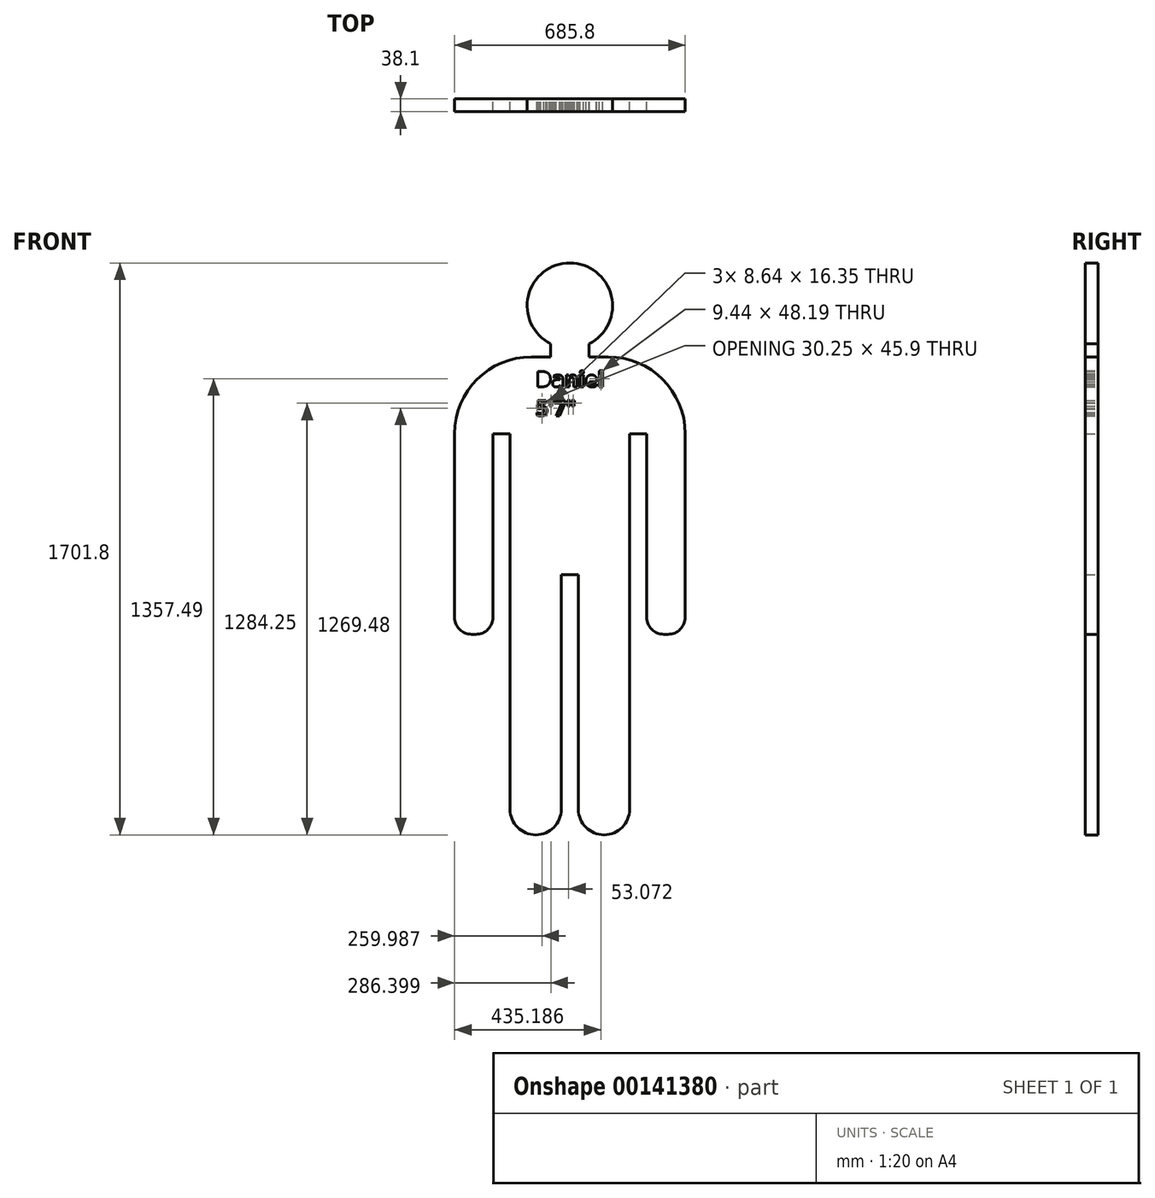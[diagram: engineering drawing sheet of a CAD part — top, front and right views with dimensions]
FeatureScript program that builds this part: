
annotation { "Feature Type Name" : "Feature", "Feature Type Description" : "" }
export const myFeature = defineFeature(function(context is Context, id is Id, definition is map)
    precondition{}
    {
        {
            var Q0;
            Q0=qCreatedBy(makeId("Front.planeOp"),FACE);
            var sketch = newSketch(context, id + "F0", { "sketchPlane" : qUnion([Q0])});
            skArc(sketch, "E0", {"start": v(48.02, 798.98) * mm, "mid": v(-9.13, 1039.4) * mm, "end": v(-66.28, 798.98) * mm});
            skLineSegment(sketch, "E1.bottom", {"start": v(-123.43, 760) * mm, "end": v(-66.28, 760) * mm});
            skLineSegment(sketch, "E1.top", {"start": v(-110.73, -662.4) * mm, "end": v(-110.73, -662.4) * mm});
            skLineSegment(sketch, "E1.left", {"start": v(-352.03, 531.4) * mm, "end": v(-352.03, -14.7) * mm});
            skLineSegment(sketch, "E1.right", {"start": v(333.77, 531.4) * mm, "end": v(333.77, -14.7) * mm});
            skPoint(sketch, "E2.visualSharp", {"position": v(-352.03, 760) * mm});
            skArc(sketch, "E2.filletArc", {"start": v(-345.68, 760) * mm, "mid": v(-350.17, 758.14) * mm, "end": v(-352.03, 753.65) * mm});
            skArc(sketch, "E3.filletArc", {"start": v(-123.43, 760) * mm, "mid": v(-285.08, 693.04) * mm, "end": v(-352.03, 531.4) * mm});
            skPoint(sketch, "E4.visualSharp", {"position": v(333.77, 760) * mm});
            skArc(sketch, "E4.filletArc", {"start": v(333.77, 531.4) * mm, "mid": v(266.81, 693.04) * mm, "end": v(105.17, 760) * mm});
            skLineSegment(sketch, "E5", {"start": v(-34.53, -586.2) * mm, "end": v(-34.53, 112.3) * mm});
            skLineSegment(sketch, "E6", {"start": v(16.27, 112.3) * mm, "end": v(16.27, -586.2) * mm});
            skLineSegment(sketch, "E7", {"start": v(-186.93, 531.4) * mm, "end": v(-186.93, -586.2) * mm});
            skLineSegment(sketch, "E8", {"start": v(168.67, 531.4) * mm, "end": v(168.67, -586.2) * mm});
            skLineSegment(sketch, "E9", {"start": v(-301.23, -65.5) * mm, "end": v(-288.53, -65.5) * mm});
            skLineSegment(sketch, "E10", {"start": v(-237.73, -14.7) * mm, "end": v(-237.73, 531.4) * mm});
            skLineSegment(sketch, "E11", {"start": v(-237.73, 531.4) * mm, "end": v(-186.93, 531.4) * mm});
            skLineSegment(sketch, "E12", {"start": v(168.67, 531.4) * mm, "end": v(219.47, 531.4) * mm});
            skLineSegment(sketch, "E13", {"start": v(219.47, 531.4) * mm, "end": v(219.47, -14.7) * mm});
            skLineSegment(sketch, "E14", {"start": v(270.27, -65.5) * mm, "end": v(282.97, -65.5) * mm});
            skPoint(sketch, "E15.orphan", {"position": v(-352.03, -662.4) * mm});
            skLineSegment(sketch, "E16.trimOffspring", {"start": v(92.47, -662.4) * mm, "end": v(92.47, -662.4) * mm});
            skPoint(sketch, "E17.orphan", {"position": v(333.77, -662.4) * mm});
            skLineSegment(sketch, "E18", {"start": v(16.27, 112.3) * mm, "end": v(-34.53, 112.3) * mm});
            skPoint(sketch, "E19.visualSharp", {"position": v(-352.03, -65.5) * mm});
            skArc(sketch, "E19.filletArc", {"start": v(-352.03, -14.7) * mm, "mid": v(-337.15, -50.62) * mm, "end": v(-301.23, -65.5) * mm});
            skPoint(sketch, "E20.visualSharp", {"position": v(-237.73, -65.5) * mm});
            skArc(sketch, "E20.filletArc", {"start": v(-288.53, -65.5) * mm, "mid": v(-252.6, -50.62) * mm, "end": v(-237.73, -14.7) * mm});
            skPoint(sketch, "E21.visualSharp", {"position": v(219.47, -65.5) * mm});
            skArc(sketch, "E21.filletArc", {"start": v(219.47, -14.7) * mm, "mid": v(234.35, -50.62) * mm, "end": v(270.27, -65.5) * mm});
            skPoint(sketch, "E22.visualSharp", {"position": v(333.77, -65.5) * mm});
            skArc(sketch, "E22.filletArc", {"start": v(282.97, -65.5) * mm, "mid": v(318.9, -50.62) * mm, "end": v(333.77, -14.7) * mm});
            skPoint(sketch, "E23.visualSharp", {"position": v(-186.93, -662.4) * mm});
            skArc(sketch, "E23.filletArc", {"start": v(-186.93, -586.2) * mm, "mid": v(-164.61, -640.08) * mm, "end": v(-110.73, -662.4) * mm});
            skPoint(sketch, "E24.visualSharp", {"position": v(-34.53, -662.4) * mm});
            skArc(sketch, "E24.filletArc", {"start": v(-110.73, -662.4) * mm, "mid": v(-56.85, -640.08) * mm, "end": v(-34.53, -586.2) * mm});
            skPoint(sketch, "E25.visualSharp", {"position": v(16.27, -662.4) * mm});
            skArc(sketch, "E25.filletArc", {"start": v(16.27, -586.2) * mm, "mid": v(38.59, -640.08) * mm, "end": v(92.47, -662.4) * mm});
            skPoint(sketch, "E26.visualSharp", {"position": v(168.67, -662.4) * mm});
            skArc(sketch, "E26.filletArc", {"start": v(92.47, -662.4) * mm, "mid": v(146.35, -640.08) * mm, "end": v(168.67, -586.2) * mm});
            skLineSegment(sketch, "E27", {"start": v(48.02, 760) * mm, "end": v(105.17, 760) * mm});
            skPoint(sketch, "E28.start.orphan", {"position": v(-9.13, 760) * mm});
            skLineSegment(sketch, "E29", {"start": v(-66.28, 798.98) * mm, "end": v(-66.28, 760) * mm});
            skLineSegment(sketch, "E30", {"start": v(48.02, 760) * mm, "end": v(48.02, 798.98) * mm});
            skText(sketch, "E31", { "text": "Daniel\n5\'7\"\n", "fontName": "OpenSans-Bold.ttf"});
            const initialGuessF0  = {"E31": [-0.11027, 0.671, 1, 0, 0.04566]};
            skSetInitialGuess(sketch, initialGuessF0);
            skSolve(sketch);
        }
        {
            var Q0;
            Q0 = qSketchRegion(id + "F0", true);
            extrude(context, id + "F1", {"entities" : qUnion([Q0]), "depth" : 38.1 * mm});
        }
    });
